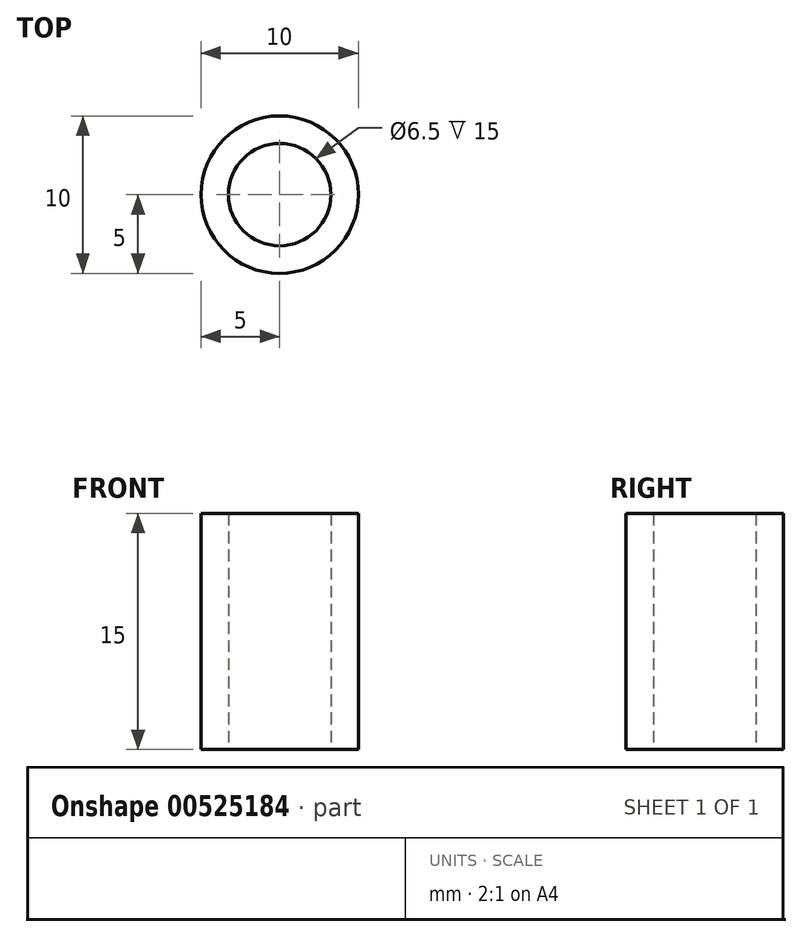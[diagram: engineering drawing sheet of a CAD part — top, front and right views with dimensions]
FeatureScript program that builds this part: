
annotation { "Feature Type Name" : "Feature", "Feature Type Description" : "" }
export const myFeature = defineFeature(function(context is Context, id is Id, definition is map)
    precondition{}
    {
        {
            var Q0;
            Q0=qCreatedBy(makeId("Top.planeOp"),FACE);
            var sketch = newSketch(context, id + "F0", { "sketchPlane" : qUnion([Q0])});
            skCircle(sketch, "E0", {"center": v(0, 0) * mm, "radius": 5 * mm});
            skCircle(sketch, "E1", {"center": v(0, 0) * mm, "radius": 3.25 * mm});
            skSolve(sketch);
        }
        {
            var Q0;
            Q0 = qSketchRegion(id + "F0", true);
            extrude(context, id + "F1", {"entities" : qUnion([Q0]), "depth" : 15 * mm, "offsetDistance" : 25 * mm});
        }
    });
